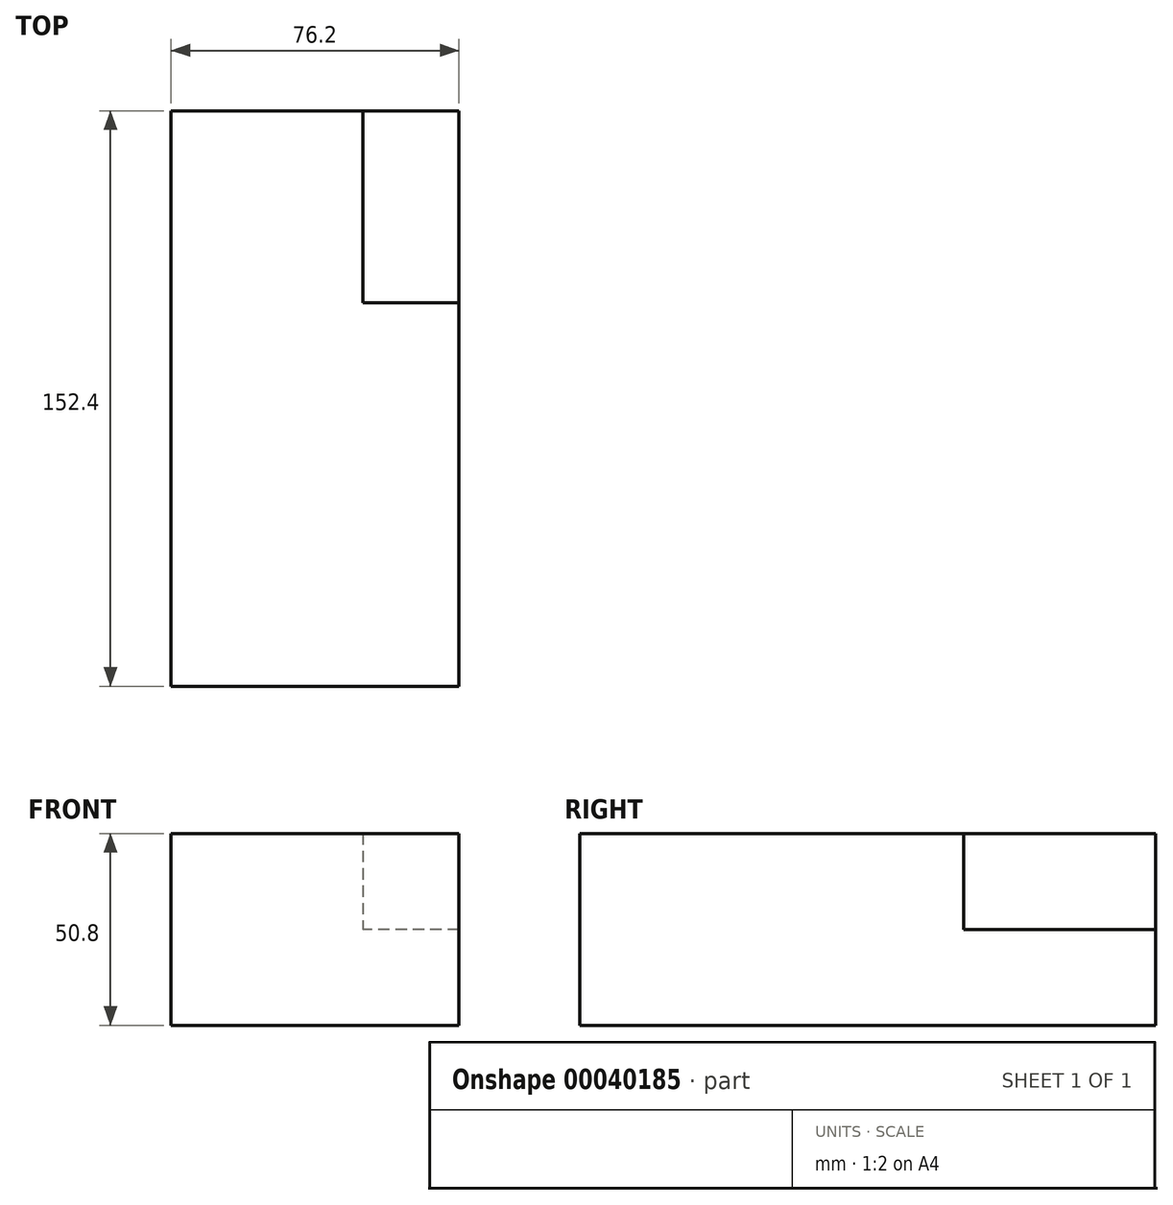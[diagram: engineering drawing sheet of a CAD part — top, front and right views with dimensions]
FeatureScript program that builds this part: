
annotation { "Feature Type Name" : "Feature", "Feature Type Description" : "" }
export const myFeature = defineFeature(function(context is Context, id is Id, definition is map)
    precondition{}
    {
        {
            var Q0;
            Q0=qCreatedBy(makeId("Top.planeOp"),FACE);
            var sketch = newSketch(context, id + "F0", { "sketchPlane" : qUnion([Q0])});
            skLineSegment(sketch, "E0.bottom", {"start": v(36.73, -51.22) * mm, "end": v(-39.47, -51.22) * mm});
            skLineSegment(sketch, "E0.top", {"start": v(36.73, 101.18) * mm, "end": v(-39.47, 101.18) * mm});
            skLineSegment(sketch, "E0.left", {"start": v(36.73, -51.22) * mm, "end": v(36.73, 101.18) * mm});
            skLineSegment(sketch, "E0.right", {"start": v(-39.47, -51.22) * mm, "end": v(-39.47, 101.18) * mm});
            skSolve(sketch);
        }
        {
            var Q0;
            Q0 = qSketchRegion(id + "F0", true);
            extrude(context, id + "F1", {"entities" : qUnion([Q0]), "depth" : 25.4 * mm});
        }
        {
            var Q0;
            Q0=makeQuery(id+"F1.opExtrude","CAP_FACE",FACE,{"disambiguationData":[OSD([sQuery(id+"F0.wireOp",EDGE,"E0.bottom"),sQuery(id+"F0.wireOp",EDGE,"E0.top"),sQuery(id+"F0.wireOp",EDGE,"E0.left"),sQuery(id+"F0.wireOp",EDGE,"E0.right")])],"isStart":false});
            var sketch = newSketch(context, id + "F2", { "sketchPlane" : qUnion([Q0])});
            skLineSegment(sketch, "E1.bottom", {"start": v(-39.47, 101.18) * mm, "end": v(11.33, 101.18) * mm});
            skLineSegment(sketch, "E1.top", {"start": v(-39.47, -51.22) * mm, "end": v(11.33, -51.22) * mm});
            skLineSegment(sketch, "E1.left", {"start": v(-39.47, 101.18) * mm, "end": v(-39.47, -51.22) * mm});
            skLineSegment(sketch, "E1.right", {"start": v(11.33, 101.18) * mm, "end": v(11.33, -51.22) * mm});
            skSolve(sketch);
        }
        {
            var Q0;
            Q0 = qSketchRegion(id + "F2", true);
            extrude(context, id + "F3", {"entities" : qUnion([Q0]), "operationType" : NewBodyOperationType.ADD, "depth" : 25.4 * mm});
        }
        {
            var Q0;
            Q0=makeQuery(id+"F1.opExtrude","CAP_FACE",FACE,{"disambiguationData":[OSD([sQuery(id+"F0.wireOp",EDGE,"E0.bottom"),sQuery(id+"F0.wireOp",EDGE,"E0.top"),sQuery(id+"F0.wireOp",EDGE,"E0.left"),sQuery(id+"F0.wireOp",EDGE,"E0.right")])],"isStart":false});
            var sketch = newSketch(context, id + "F4", { "sketchPlane" : qUnion([Q0])});
            skLineSegment(sketch, "E2.bottom", {"start": v(36.73, -51.22) * mm, "end": v(11.33, -51.22) * mm});
            skLineSegment(sketch, "E2.top", {"start": v(36.73, 50.38) * mm, "end": v(11.33, 50.38) * mm});
            skLineSegment(sketch, "E2.left", {"start": v(36.73, -51.22) * mm, "end": v(36.73, 50.38) * mm});
            skLineSegment(sketch, "E2.right", {"start": v(11.33, -51.22) * mm, "end": v(11.33, 50.38) * mm});
            skSolve(sketch);
        }
        {
            var Q0;
            Q0 = qSketchRegion(id + "F4", true);
            extrude(context, id + "F5", {"entities" : qUnion([Q0]), "operationType" : NewBodyOperationType.ADD, "depth" : 25.4 * mm});
        }
    });
